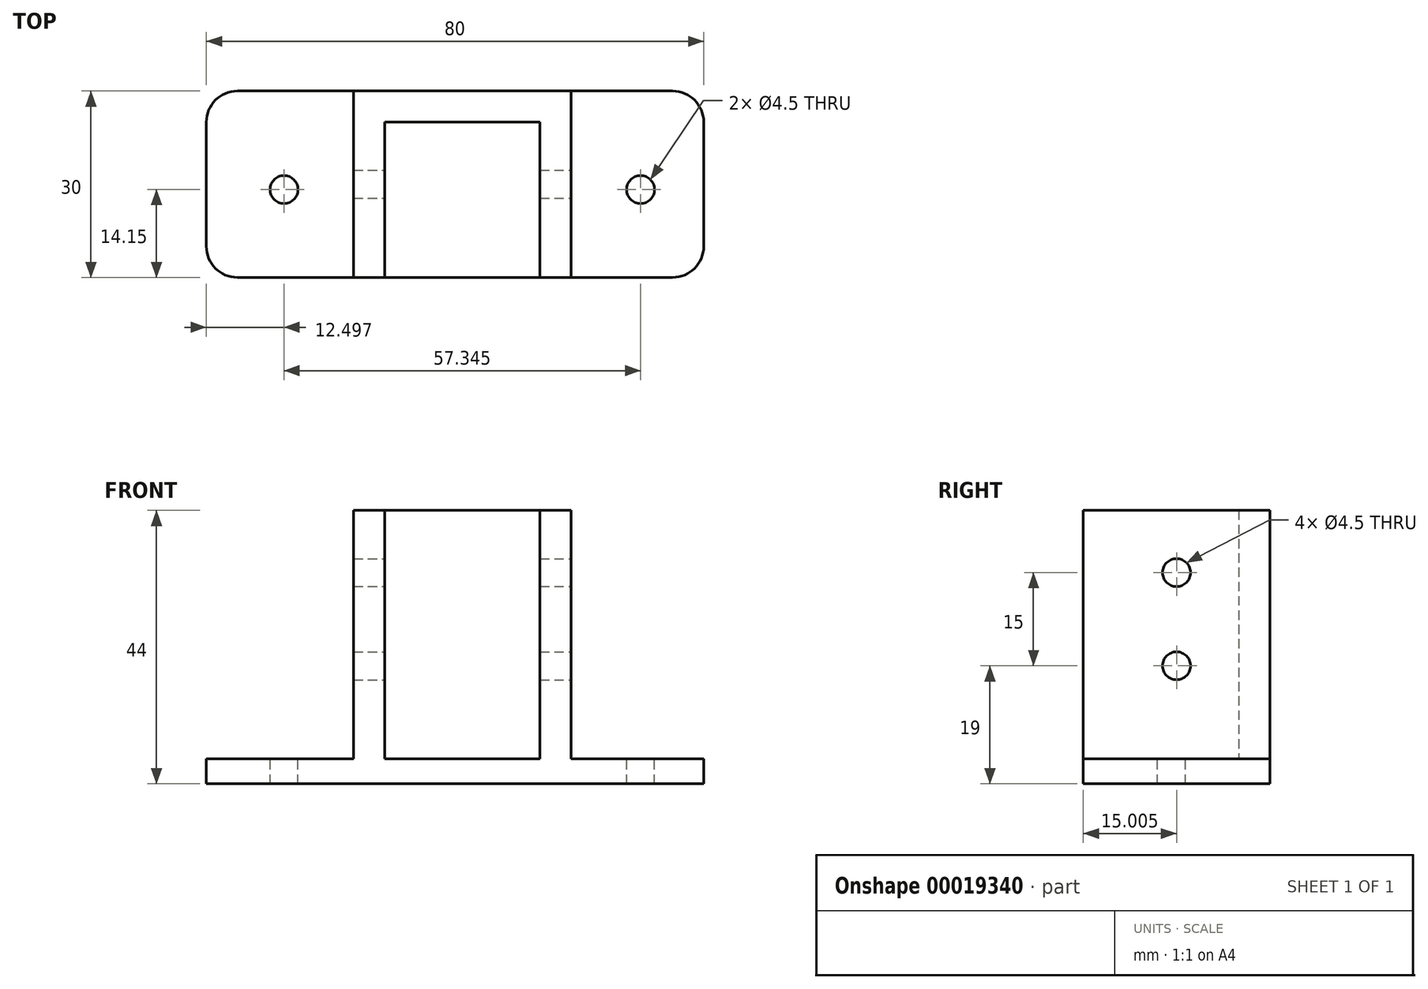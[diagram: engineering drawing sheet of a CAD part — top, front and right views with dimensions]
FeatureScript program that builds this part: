
annotation { "Feature Type Name" : "Feature", "Feature Type Description" : "" }
export const myFeature = defineFeature(function(context is Context, id is Id, definition is map)
    precondition{}
    {
        {
            var Q0;
            Q0=qCreatedBy(makeId("Top.planeOp"),FACE);
            var sketch = newSketch(context, id + "F0", { "sketchPlane" : qUnion([Q0])});
            skLineSegment(sketch, "E0.bottom", {"start": v(-36.17, 15.85) * mm, "end": v(33.83, 15.85) * mm});
            skLineSegment(sketch, "E0.top", {"start": v(-36.17, -14.15) * mm, "end": v(33.83, -14.15) * mm});
            skLineSegment(sketch, "E0.left", {"start": v(-41.17, 10.85) * mm, "end": v(-41.17, -9.15) * mm});
            skLineSegment(sketch, "E0.right", {"start": v(38.83, 10.85) * mm, "end": v(38.83, -9.15) * mm});
            skPoint(sketch, "E1.visualSharp", {"position": v(-41.17, 15.85) * mm});
            skArc(sketch, "E1.filletArc", {"start": v(-36.17, 15.85) * mm, "mid": v(-39.7, 14.4) * mm, "end": v(-41.17, 10.85) * mm});
            skPoint(sketch, "E2.visualSharp", {"position": v(-41.17, -14.15) * mm});
            skArc(sketch, "E2.filletArc", {"start": v(-41.17, -9.15) * mm, "mid": v(-39.7, -12.68) * mm, "end": v(-36.17, -14.15) * mm});
            skPoint(sketch, "E3.visualSharp", {"position": v(38.83, -14.15) * mm});
            skArc(sketch, "E3.filletArc", {"start": v(33.83, -14.15) * mm, "mid": v(37.36, -12.68) * mm, "end": v(38.83, -9.15) * mm});
            skPoint(sketch, "E4.visualSharp", {"position": v(38.83, 15.85) * mm});
            skArc(sketch, "E4.filletArc", {"start": v(38.83, 10.85) * mm, "mid": v(37.36, 14.4) * mm, "end": v(33.83, 15.85) * mm});
            skSolve(sketch);
        }
        {
            var Q0;
            Q0=makeQuery(id+"F0.imprint","IMPRINT",FACE,{"disambiguationData":[TD([[makeQuery(id+"F0.imprint","IMPRINT",EDGE,{"derivedFrom":sQuery(id+"F0.wireOp",EDGE,"E0.bottom")}),-1.0]])]});
            extrude(context, id + "F1", {"entities" : qUnion([Q0]), "depth" : 4 * mm});
        }
        {
            var Q0;
            Q0=makeQuery(id+"F1.opExtrude","CAP_FACE",FACE,{"disambiguationData":[OSD([sQuery(id+"F0.wireOp",EDGE,"E0.bottom"),sQuery(id+"F0.wireOp",EDGE,"E0.top"),sQuery(id+"F0.wireOp",EDGE,"E0.left"),sQuery(id+"F0.wireOp",EDGE,"E0.right"),sQuery(id+"F0.wireOp",EDGE,"E1.filletArc"),sQuery(id+"F0.wireOp",EDGE,"E2.filletArc"),sQuery(id+"F0.wireOp",EDGE,"E3.filletArc"),sQuery(id+"F0.wireOp",EDGE,"E4.filletArc")])],"isStart":false});
            var sketch = newSketch(context, id + "F2", { "sketchPlane" : qUnion([Q0])});
            skLineSegment(sketch, "E5", {"start": v(-12.5, -14.15) * mm, "end": v(-12.5, 10.85) * mm});
            skLineSegment(sketch, "E6", {"start": v(-12.5, 10.85) * mm, "end": v(12.5, 10.85) * mm});
            skLineSegment(sketch, "E7", {"start": v(12.5, 10.85) * mm, "end": v(12.5, -14.15) * mm});
            skLineSegment(sketch, "E8.0", {"start": v(17.5, 15.85) * mm, "end": v(17.5, -14.15) * mm});
            skLineSegment(sketch, "E8.1", {"start": v(-17.5, 15.85) * mm, "end": v(17.5, 15.85) * mm});
            skLineSegment(sketch, "E8.2", {"start": v(-17.5, -14.15) * mm, "end": v(-17.5, 15.85) * mm});
            skLineSegment(sketch, "E9", {"start": v(-17.5, -14.15) * mm, "end": v(-12.5, -14.15) * mm});
            skLineSegment(sketch, "E10", {"start": v(12.5, -14.15) * mm, "end": v(17.5, -14.15) * mm});
            skSolve(sketch);
        }
        {
            var Q0;
            Q0=makeQuery(id+"F2.imprint","IMPRINT",FACE,{"disambiguationData":[TD([[makeQuery(id+"F2.imprint","IMPRINT",EDGE,{"derivedFrom":sQuery(id+"F2.wireOp",EDGE,"E5")}),1.0]])]});
            extrude(context, id + "F3", {"entities" : qUnion([Q0]), "operationType" : NewBodyOperationType.ADD, "depth" : 40 * mm});
        }
        {
            var Q0;
            {var subQ0=sQuery(id+"F0.wireOp",EDGE,"E0.bottom");var subQ1=sQuery(id+"F0.wireOp",EDGE,"E0.top");var subQ2=sQuery(id+"F0.wireOp",EDGE,"E0.left");var subQ3=sQuery(id+"F0.wireOp",EDGE,"E1.filletArc");var subQ4=sQuery(id+"F0.wireOp",EDGE,"E2.filletArc");Q0=makeQuery(id+"F3.boolean.opBoolean","SPLIT",FACE,{"disambiguationData":[TD([makeQuery(id+"F1.opExtrude","SWEPT_FACE",FACE,{"disambiguationData":[OSD([subQ2])]})])],"derivedFrom":makeQuery(id+"F1.opExtrude","CAP_FACE",FACE,{"disambiguationData":[OSD([subQ0,subQ1,subQ2,sQuery(id+"F0.wireOp",EDGE,"E0.right"),subQ3,subQ4,sQuery(id+"F0.wireOp",EDGE,"E3.filletArc"),sQuery(id+"F0.wireOp",EDGE,"E4.filletArc")])],"isStart":false})});}
            var sketch = newSketch(context, id + "F4", { "sketchPlane" : qUnion([Q0])});
            skCircle(sketch, "E11", {"center": v(-28.67, 0) * mm, "radius": 2.25 * mm});
            skCircle(sketch, "E12.MirrorC", {"center": v(28.67, 0) * mm, "radius": 2.25 * mm});
            skSolve(sketch);
        }
        {
            var Q0;
            Q0 = qSketchRegion(id + "F4", true);
            extrude(context, id + "F5", {"entities" : qUnion([Q0]), "operationType" : NewBodyOperationType.REMOVE, "oppositeDirection" : true, "depth" : 25 * mm});
        }
        {
            var Q0;
            Q0=makeQuery(id+"F3.opExtrude","SWEPT_FACE",FACE,{"disambiguationData":[OSD([sQuery(id+"F2.wireOp",EDGE,"E8.0")])]});
            var sketch = newSketch(context, id + "F6", { "sketchPlane" : qUnion([Q0])});
            skCircle(sketch, "E13", {"center": v(0.85, 34) * mm, "radius": 2.25 * mm});
            skCircle(sketch, "E14.0.1.0", {"center": v(0.85, 19) * mm, "radius": 2.25 * mm});
            skLineSegment(sketch, "E14.direction1", {"start": v(0.85, 34) * mm, "end": v(25.85, 34) * mm, "construction": true});
            skLineSegment(sketch, "E14.direction2", {"start": v(0.85, 34) * mm, "end": v(0.85, 19) * mm, "construction": true});
            skSolve(sketch);
        }
        {
            var Q0;
            Q0 = qSketchRegion(id + "F6", true);
            extrude(context, id + "F7", {"entities" : qUnion([Q0]), "operationType" : NewBodyOperationType.REMOVE, "endBound" : BoundingType.THROUGH_ALL, "oppositeDirection" : true, "depth" : 25 * mm});
        }
    });
